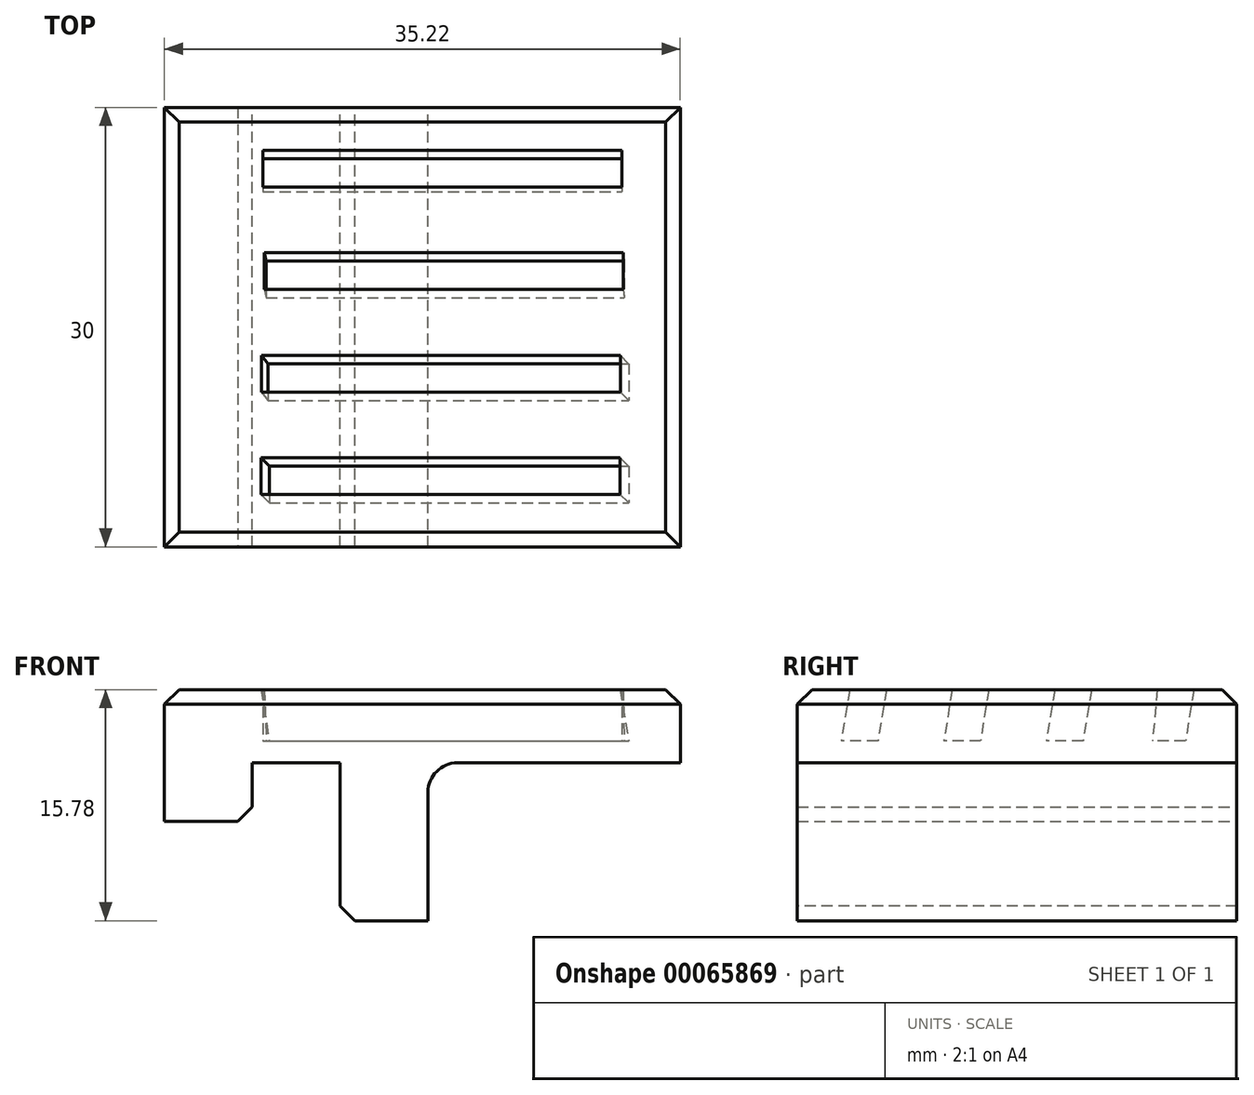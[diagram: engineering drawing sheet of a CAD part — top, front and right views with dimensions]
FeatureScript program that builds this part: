
annotation { "Feature Type Name" : "Feature", "Feature Type Description" : "" }
export const myFeature = defineFeature(function(context is Context, id is Id, definition is map)
    precondition{}
    {
        {
            var Q0;
            Q0=qCreatedBy(makeId("Front.planeOp"),FACE);
            var sketch = newSketch(context, id + "F0", { "sketchPlane" : qUnion([Q0])});
            skLineSegment(sketch, "E0", {"start": v(0, 0) * mm, "end": v(-6, 0) * mm});
            skLineSegment(sketch, "E1", {"start": v(-6, 0) * mm, "end": v(-6, 10.78) * mm});
            skLineSegment(sketch, "E2", {"start": v(-6, 10.78) * mm, "end": v(-12, 10.78) * mm});
            skLineSegment(sketch, "E3", {"start": v(-12, 10.78) * mm, "end": v(-12, 6.78) * mm});
            skLineSegment(sketch, "E4", {"start": v(-12, 6.78) * mm, "end": v(-18, 6.78) * mm});
            skLineSegment(sketch, "E5", {"start": v(-18, 6.78) * mm, "end": v(-18, 15.78) * mm});
            skLineSegment(sketch, "E6", {"start": v(-18, 15.78) * mm, "end": v(4.67, 15.78) * mm});
            skLineSegment(sketch, "E7", {"start": v(4.67, 15.78) * mm, "end": v(17.22, 15.78) * mm});
            skLineSegment(sketch, "E8", {"start": v(17.22, 15.78) * mm, "end": v(17.22, 10.78) * mm});
            skLineSegment(sketch, "E9", {"start": v(17.22, 10.78) * mm, "end": v(0, 10.78) * mm});
            skLineSegment(sketch, "E10", {"start": v(0, 10.78) * mm, "end": v(0, 0) * mm});
            skSolve(sketch);
        }
        {
            var Q0;
            Q0=makeQuery(id+"F0.imprint","IMPRINT",FACE,{"disambiguationData":[TD([[makeQuery(id+"F0.imprint","IMPRINT",EDGE,{"derivedFrom":sQuery(id+"F0.wireOp",EDGE,"E0")}),-1.0]])]});
            extrude(context, id + "F1", {"entities" : qUnion([Q0]), "depth" : 30 * mm});
        }
        {
            var Q0;
            Q0=makeQuery(id+"F1.opExtrude","CAP_EDGE",EDGE,{"disambiguationData":[OSD([sQuery(id+"F0.wireOp",EDGE,"E6"),sQuery(id+"F0.wireOp",EDGE,"E7")])],"isStart":false});
            var Q1;
            Q1=makeQuery(id+"F1.opExtrude","SWEPT_EDGE",EDGE,{"disambiguationData":[OSD([sQuery(id+"F0.wireOp",EDGE,"E7"),sQuery(id+"F0.wireOp",EDGE,"E8")])]});
            var Q2;
            Q2=makeQuery(id+"F1.opExtrude","CAP_EDGE",EDGE,{"disambiguationData":[OSD([sQuery(id+"F0.wireOp",EDGE,"E6"),sQuery(id+"F0.wireOp",EDGE,"E7")])],"isStart":true});
            var Q3;
            Q3=makeQuery(id+"F1.opExtrude","SWEPT_EDGE",EDGE,{"disambiguationData":[OSD([sQuery(id+"F0.wireOp",EDGE,"E5"),sQuery(id+"F0.wireOp",EDGE,"E6")])]});
            var Q4;
            Q4=makeQuery(id+"F1.opExtrude","SWEPT_EDGE",EDGE,{"disambiguationData":[OSD([sQuery(id+"F0.wireOp",EDGE,"E3"),sQuery(id+"F0.wireOp",EDGE,"E4")])]});
            var Q5;
            Q5=makeQuery(id+"F1.opExtrude","SWEPT_EDGE",EDGE,{"disambiguationData":[OSD([sQuery(id+"F0.wireOp",EDGE,"E0"),sQuery(id+"F0.wireOp",EDGE,"E1")])]});
            chamfer(context, id + "F2", {"entities" : qUnion([Q0, Q1, Q2, Q3, Q4, Q5]), "width" : 1 * mm, "tangentPropagation" : true});
        }
        {
            var Q0;
            Q0=makeQuery(id+"F1.opExtrude","SWEPT_EDGE",EDGE,{"disambiguationData":[OSD([sQuery(id+"F0.wireOp",EDGE,"E9"),sQuery(id+"F0.wireOp",EDGE,"E10")])]});
            fillet(context, id + "F3", {"entities" : qUnion([Q0]), "radius" : 2 * mm, "tangentPropagation" : true, "allowEdgeOverflow" : false});
        }
        {
            var Q0;
            Q0=makeQuery(id+"F1.opExtrude","SWEPT_FACE",FACE,{"disambiguationData":[OSD([sQuery(id+"F0.wireOp",EDGE,"E6"),sQuery(id+"F0.wireOp",EDGE,"E7")])]});
            var sketch = newSketch(context, id + "F4", { "sketchPlane" : qUnion([Q0])});
            skLineSegment(sketch, "E11.bottom", {"start": v(-11.28, -2.93) * mm, "end": v(13.22, -2.93) * mm});
            skLineSegment(sketch, "E11.top", {"start": v(-11.28, -5.43) * mm, "end": v(13.22, -5.43) * mm});
            skLineSegment(sketch, "E11.left", {"start": v(-11.28, -2.93) * mm, "end": v(-11.28, -5.43) * mm});
            skLineSegment(sketch, "E11.right", {"start": v(13.22, -2.93) * mm, "end": v(13.22, -5.43) * mm});
            skLineSegment(sketch, "E12.bottom", {"start": v(-11.17, -9.93) * mm, "end": v(13.33, -9.93) * mm});
            skLineSegment(sketch, "E12.top", {"start": v(-11.17, -12.43) * mm, "end": v(13.33, -12.43) * mm});
            skLineSegment(sketch, "E12.left", {"start": v(-11.17, -9.93) * mm, "end": v(-11.17, -12.43) * mm});
            skLineSegment(sketch, "E12.right", {"start": v(13.33, -9.93) * mm, "end": v(13.33, -12.43) * mm});
            skLineSegment(sketch, "E13.bottom", {"start": v(-11.37, -16.93) * mm, "end": v(13.13, -16.93) * mm});
            skLineSegment(sketch, "E13.top", {"start": v(-11.37, -19.43) * mm, "end": v(13.13, -19.43) * mm});
            skLineSegment(sketch, "E13.left", {"start": v(-11.37, -16.93) * mm, "end": v(-11.37, -19.43) * mm});
            skLineSegment(sketch, "E13.right", {"start": v(13.13, -16.93) * mm, "end": v(13.13, -19.43) * mm});
            skLineSegment(sketch, "E14.bottom", {"start": v(-11.4, -23.93) * mm, "end": v(13.1, -23.93) * mm});
            skLineSegment(sketch, "E14.top", {"start": v(-11.4, -26.43) * mm, "end": v(13.1, -26.43) * mm});
            skLineSegment(sketch, "E14.left", {"start": v(-11.4, -23.93) * mm, "end": v(-11.4, -26.43) * mm});
            skLineSegment(sketch, "E14.right", {"start": v(13.1, -23.93) * mm, "end": v(13.1, -26.43) * mm});
            skSolve(sketch);
        }
        {
            var Q0;
            Q0=makeQuery(id+"F4.imprint","IMPRINT",FACE,{"disambiguationData":[TD([[makeQuery(id+"F4.imprint","IMPRINT",EDGE,{"derivedFrom":sQuery(id+"F4.wireOp",EDGE,"E11.bottom")}),-1.0]])]});
            cPlane(context, id + "F5", {"entities" : qUnion([Q0]), "cplaneType" : CPlaneType.OFFSET, "offset" : 3.5 * mm, "oppositeDirection" : true, "width" : 150 * mm, "height" : 150 * mm});
        }
        {
            var Q0;
            Q0=qCreatedBy(id+"F5.planeOp",FACE);
            var sketch = newSketch(context, id + "F6", { "sketchPlane" : qUnion([Q0])});
            skLineSegment(sketch, "E15.bottom", {"start": v(-11.28, -3.5) * mm, "end": v(13.22, -3.5) * mm});
            skLineSegment(sketch, "E15.top", {"start": v(-11.28, -5.75) * mm, "end": v(13.22, -5.75) * mm});
            skLineSegment(sketch, "E15.left", {"start": v(-11.28, -3.5) * mm, "end": v(-11.28, -5.75) * mm});
            skLineSegment(sketch, "E15.right", {"start": v(13.22, -3.5) * mm, "end": v(13.22, -5.75) * mm});
            skLineSegment(sketch, "E16.bottom", {"start": v(-11.04, -10.5) * mm, "end": v(13.4, -10.5) * mm});
            skLineSegment(sketch, "E16.top", {"start": v(-11.04, -13) * mm, "end": v(13.4, -13) * mm});
            skLineSegment(sketch, "E16.left", {"start": v(-11.04, -10.5) * mm, "end": v(-11.04, -13) * mm});
            skLineSegment(sketch, "E16.right", {"start": v(13.4, -10.5) * mm, "end": v(13.4, -13) * mm});
            skLineSegment(sketch, "E17.bottom", {"start": v(-10.94, -17.5) * mm, "end": v(13.7, -17.5) * mm});
            skLineSegment(sketch, "E17.top", {"start": v(-10.94, -20) * mm, "end": v(13.7, -20) * mm});
            skLineSegment(sketch, "E17.left", {"start": v(-10.94, -17.5) * mm, "end": v(-10.94, -20) * mm});
            skLineSegment(sketch, "E17.right", {"start": v(13.7, -17.5) * mm, "end": v(13.7, -20) * mm});
            skLineSegment(sketch, "E18.bottom", {"start": v(-10.84, -24.5) * mm, "end": v(13.7, -24.5) * mm});
            skLineSegment(sketch, "E18.top", {"start": v(-10.84, -27) * mm, "end": v(13.7, -27) * mm});
            skLineSegment(sketch, "E18.left", {"start": v(-10.84, -24.5) * mm, "end": v(-10.84, -27) * mm});
            skLineSegment(sketch, "E18.right", {"start": v(13.7, -24.5) * mm, "end": v(13.7, -27) * mm});
            skSolve(sketch);
        }
        {
            var Q1;
            Q1=makeQuery(id+"F4.imprint","IMPRINT",FACE,{"disambiguationData":[TD([[makeQuery(id+"F4.imprint","IMPRINT",EDGE,{"derivedFrom":sQuery(id+"F4.wireOp",EDGE,"E14.bottom")}),-1.0]])]});
            var Q2;
            Q2=makeQuery(id+"F6.imprint","IMPRINT",FACE,{"disambiguationData":[TD([[makeQuery(id+"F6.imprint","IMPRINT",EDGE,{"derivedFrom":sQuery(id+"F6.wireOp",EDGE,"E18.bottom")}),-1.0]])]});
            loft(context, id + "F7", {"operationType" : NewBodyOperationType.REMOVE, "sheetProfilesArray" : [{ "sheetProfileEntities" : qUnion([Q1]) }, { "sheetProfileEntities" : qUnion([Q2]) }]});
        }
        {
            var Q1;
            Q1=makeQuery(id+"F4.imprint","IMPRINT",FACE,{"disambiguationData":[TD([[makeQuery(id+"F4.imprint","IMPRINT",EDGE,{"derivedFrom":sQuery(id+"F4.wireOp",EDGE,"E13.bottom")}),-1.0]])]});
            var Q2;
            Q2=makeQuery(id+"F6.imprint","IMPRINT",FACE,{"disambiguationData":[TD([[makeQuery(id+"F6.imprint","IMPRINT",EDGE,{"derivedFrom":sQuery(id+"F6.wireOp",EDGE,"E17.bottom")}),-1.0]])]});
            loft(context, id + "F8", {"operationType" : NewBodyOperationType.REMOVE, "sheetProfilesArray" : [{ "sheetProfileEntities" : qUnion([Q1]) }, { "sheetProfileEntities" : qUnion([Q2]) }]});
        }
        {
            var Q1;
            Q1=makeQuery(id+"F4.imprint","IMPRINT",FACE,{"disambiguationData":[TD([[makeQuery(id+"F4.imprint","IMPRINT",EDGE,{"derivedFrom":sQuery(id+"F4.wireOp",EDGE,"E12.bottom")}),-1.0]])]});
            var Q2;
            Q2=makeQuery(id+"F6.imprint","IMPRINT",FACE,{"disambiguationData":[TD([[makeQuery(id+"F6.imprint","IMPRINT",EDGE,{"derivedFrom":sQuery(id+"F6.wireOp",EDGE,"E16.bottom")}),-1.0]])]});
            loft(context, id + "F9", {"operationType" : NewBodyOperationType.REMOVE, "sheetProfilesArray" : [{ "sheetProfileEntities" : qUnion([Q1]) }, { "sheetProfileEntities" : qUnion([Q2]) }]});
        }
        {
            var Q1;
            Q1=makeQuery(id+"F4.imprint","IMPRINT",FACE,{"disambiguationData":[TD([[makeQuery(id+"F4.imprint","IMPRINT",EDGE,{"derivedFrom":sQuery(id+"F4.wireOp",EDGE,"E11.bottom")}),-1.0]])]});
            var Q2;
            Q2=makeQuery(id+"F6.imprint","IMPRINT",FACE,{"disambiguationData":[TD([[makeQuery(id+"F6.imprint","IMPRINT",EDGE,{"derivedFrom":sQuery(id+"F6.wireOp",EDGE,"E15.bottom")}),-1.0]])]});
            loft(context, id + "F10", {"operationType" : NewBodyOperationType.REMOVE, "sheetProfilesArray" : [{ "sheetProfileEntities" : qUnion([Q1]) }, { "sheetProfileEntities" : qUnion([Q2]) }]});
        }
    });
